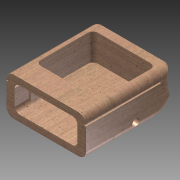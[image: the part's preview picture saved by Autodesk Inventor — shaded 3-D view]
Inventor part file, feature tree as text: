
AUTODESK INVENTOR PART (.ipt)
format: ipt  version: 2015 (Build 190159000, 159)  size: 333,312 bytes
history: native  units: in
note: dims shown in document units (in); Inventor stores cm internally (conversion verified against a paired STEP export)
features: sketch x6, extrude x6, fillet x4, hole x2
ambient origin geometry x8: Origin, YZ Plane, XZ Plane, XY Plane, X Axis, Y Axis, Z Axis, Center Point
bodies: Solid1 (feature_tree)
feature tree (18):
  sketch  "Sketch1"  dims[d0=3.17in d1=1.53in]
  extrude  "Extrusion1"  Depth=1.53in
  extrude  "Extrusion5"  Depth=0.2in
  extrude  "Extrusion3"  Depth=1.0in
  extrude  "Extrusion4"  Depth=0.837in
  extrude  "Extrusion6"  Depth=2.5in
  fillet  "Fillet1"  Radius=1.07in
  fillet  "Fillet2"  Radius=0.06in
  fillet  "Fillet3"  Radius=0.3in
  hole  "Hole1"  [1 undecoded]
  hole  "Hole2"  [1 undecoded]
  fillet  "Fillet4"  Radius=0.983in
  extrude  "Extrusion8"  Depth=3.0in TaperAngle=0.0deg
  sketch  "Sketch3"  dims[d2=3.5in d3=0.0in d9=0.2in]
  sketch  "Sketch4"  dims[d10=2.5in d11=1.0in]
  sketch  "Sketch5"  dims[d12=0.57in d13=0.0in d15=0.837in]
  sketch  "Sketch6"  dims[d16=2.28in d17=2.5in d18=1.07in d19=0.0in d20=0.06in d21=0.3in]
  sketch  "Sketch10"  dims[d23=3.0in d24=0.0in d25=0.05in d26=0.75in d27=0.983in d28=3.0in d29=0.0in d30=0.75in d31=0.3in d32=0.3in d33=0.1in d34=0.28in d35=0.28in d36=2.8in d37=0.2in d38=0.75in d39=0.375in d40=0.25in d41=0.5635in d42=0.125in d43=0.8108in d44=2.0in d45=0.3in d46=0.305in d47=0.75in d48=0.375in d49=0.25in d50=0.5635in d51=0.35in d52=0.8108in d53=0.01in d62=1.0in d63=0.0in]
note: 2 required parameter values undecoded (feature->parameter linkage not recoverable at this tier; creation-order binding heuristic only, values carry confidence <= 0.55)
